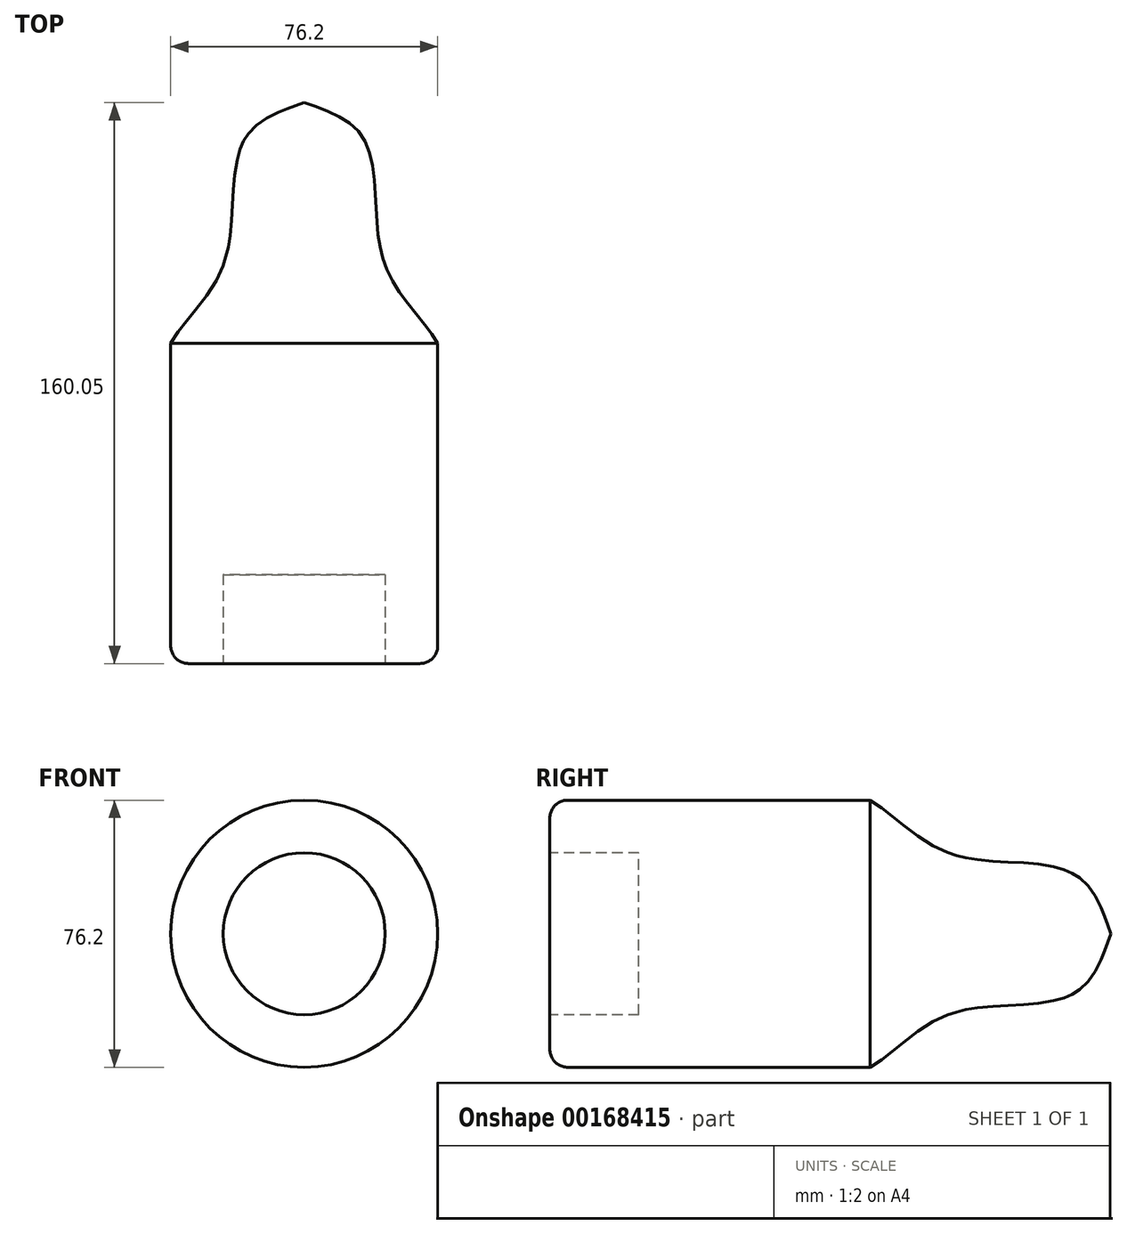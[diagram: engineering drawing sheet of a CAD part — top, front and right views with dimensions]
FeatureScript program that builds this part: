
annotation { "Feature Type Name" : "Feature", "Feature Type Description" : "" }
export const myFeature = defineFeature(function(context is Context, id is Id, definition is map)
    precondition{}
    {
        {
            var Q0;
            Q0=qCreatedBy(makeId("Front.planeOp"),FACE);
            var sketch = newSketch(context, id + "F0", { "sketchPlane" : qUnion([Q0])});
            skCircle(sketch, "E0", {"center": v(0, 0) * mm, "radius": 38.1 * mm});
            skSolve(sketch);
        }
        {
            var Q0;
            Q0 = qSketchRegion(id + "F0", true);
            extrude(context, id + "F1", {"entities" : qUnion([Q0]), "depth" : 91.44 * mm});
        }
        {
            var Q0;
            Q0=makeQuery(id+"F1.opExtrude","CAP_FACE",FACE,{"disambiguationData":[OSD([sQuery(id+"F0.wireOp",EDGE,"E0")])],"isStart":false});
            var sketch = newSketch(context, id + "F2", { "sketchPlane" : qUnion([Q0])});
            skCircle(sketch, "E1", {"center": v(0, 0) * mm, "radius": 23.1 * mm});
            skSolve(sketch);
        }
        {
            var Q0;
            Q0 = qSketchRegion(id + "F2", true);
            extrude(context, id + "F3", {"entities" : qUnion([Q0]), "operationType" : NewBodyOperationType.REMOVE, "oppositeDirection" : true, "depth" : 25.4 * mm});
        }
        {
            var Q0;
            Q0=makeQuery(id+"F1.opExtrude","CAP_EDGE",EDGE,{"disambiguationData":[OSD([sQuery(id+"F0.wireOp",EDGE,"E0")])],"isStart":false});
            fillet(context, id + "F4", {"entities" : qUnion([Q0]), "radius" : 5.08 * mm, "tangentPropagation" : true, "allowEdgeOverflow" : false});
        }
        {
            var Q0;
            Q0=qCreatedBy(makeId("Top.planeOp"),FACE);
            var sketch = newSketch(context, id + "F5", { "sketchPlane" : qUnion([Q0])});
            skLineSegment(sketch, "E2", {"start": v(0, 0) * mm, "end": v(0, 68.6) * mm});
            skFitSpline(sketch, "E3", {"points": [v(0, 68.6) * mm, v(16.42, 59.14) * mm, v(20.63, 36.2) * mm, v(25.47, 17.25) * mm, v(38.1, 0) * mm], "startDerivative": vector(78.48, -26.1) * mm, "endDerivative": vector(31.72, -55.45) * mm});
            skLineSegment(sketch, "E4", {"start": v(0, 0) * mm, "end": v(38.1, 0) * mm});
            skSolve(sketch);
        }
        {
            var Q0;
            Q0 = qSketchRegion(id + "F5", true);
            var Q1;
            Q1=sQuery(id+"F5.wireOp",EDGE,"E2");
            revolve(context, id + "F6", {"operationType" : NewBodyOperationType.ADD, "entities" : qUnion([Q0]), "axis" : qUnion([Q1]), "revolveType" : RevolveType.FULL});
        }
    });
